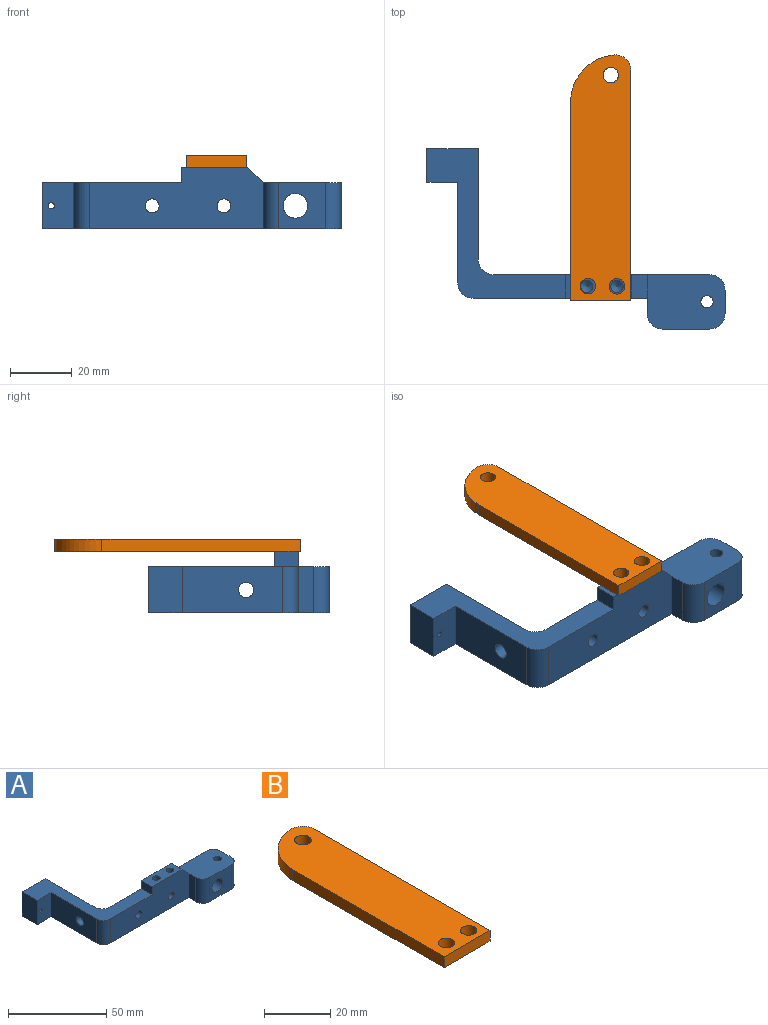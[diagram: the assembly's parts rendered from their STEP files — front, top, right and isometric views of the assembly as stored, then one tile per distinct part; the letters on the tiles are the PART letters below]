
ASSEMBLY  parts=2 mates=1
PART A: 33 faces, bbox 96.8x58.5x20 mm
  f0: plane 32.68x15mm, normal (-1,0,0), area 470.6mm2, adj f7,f8,f17,f27,f32
  f1: plane 25.29x17.65mm, normal (0,0,1), area 417.6mm2, adj f3,f6,f9,f10,f13,f14,f15,f16
  f2: plane 56.5x20mm, normal (0,-1,0), area 935.7mm2, adj f7,f8,f9,f11,f12,f13,f17,f18
  f3: plane 70.15x20mm, normal (0,1,0), area 1090.3mm2, adj f1,f7,f8,f11,f12,f13,f15,f18
  f4: plane 35.9x15mm, normal (1,0,0), area 518.8mm2, adj f5,f7,f8,f26,f32
  f5: plane 16.64x15mm, normal (0,1,0), area 233.8mm2, adj f4,f7,f8,f28,f30,f31
  f6: plane 15x7.65mm, normal (1,0,0), area 114.7mm2, adj f1,f8,f14,f15
  f7: plane 48.54x44.98mm, normal (0,0,1), area 647.4mm2, adj f0,f2,f3,f4,f5,f11,f17,f26
  f8: plane 96.79x58.54mm, normal (0,0,-1), area 1267.7mm2, adj f0,f2,f3,f4,f5,f6,f9,f10
  f9: plane 15x5mm, normal (-1,0,0), area 75mm2, adj f1,f2,f8,f16
  f10: plane 15.29x15mm, normal (0,-1,0), area 179.1mm2, adj f1,f8,f14,f16,f20
  f11: plane 7.65x5mm, normal (-1,0,0), area 38.2mm2, adj f2,f3,f7,f12
  f12: plane 21.52x7.65mm, normal (0,0,1), area 139.4mm2, adj f2,f3,f11,f13,f23,f25
  f13: plane 7.65x5mm, normal (0.71,0,0.71), area 54.1mm2, adj f1,f2,f3,f12
  f14: cylinder r=5mm len=15mm, axis (0,0,-1), area 117.8mm2, adj f1,f6,f8,f10
  f15: cylinder r=5mm len=15mm, axis (0,0,-1), area 117.8mm2, adj f1,f3,f6,f8
  f16: cylinder r=5mm len=15mm, axis (0,0,1), area 117.8mm2, adj f1,f8,f9,f10
  f17: cylinder r=5mm len=15mm, axis (0,0,-1), area 117.8mm2, adj f0,f2,f7,f8
  f18: cylinder r=2.25mm len=7.65mm, axis (0,1,0), area 108.1mm2, adj f2,f3
  f19: cylinder r=2.25mm len=7.65mm, axis (0,1,0), area 108.1mm2, adj f2,f3
  f20: cylinder r=4mm len=17.65mm, axis (0,1,0), area 443.5mm2, adj f3,f10
  f21: cylinder r=2mm len=15mm, axis (0,0,1), area 188.5mm2, adj f1,f8
  f22: cone r=0mm half-angle=59deg, axis (0,0,1), area 14.7mm2, adj f23
  f23: cylinder r=2mm len=10mm, axis (0,0,1), area 125.7mm2, adj f12,f22
  f24: cone r=0mm half-angle=59deg, axis (0,0,1), area 14.7mm2, adj f25
  f25: cylinder r=2mm len=10mm, axis (0,0,1), area 125.7mm2, adj f12,f24
  f26: cylinder r=5mm len=15mm, axis (0,0,-1), area 117.8mm2, adj f3,f4,f7,f8
  f27: plane 15x10mm, normal (0,-1,0), area 146.9mm2, adj f0,f7,f8,f28,f31
  f28: plane 15x10.86mm, normal (-1,0,0), area 162.9mm2, adj f5,f7,f8,f27
  f29: cone r=0mm half-angle=59deg, axis (0,1,0), area 14.7mm2, adj f30
  f30: cylinder r=2mm len=8mm, axis (0,1,0), area 100.5mm2, adj f5,f29
  f31: cylinder r=1mm len=10.86mm, axis (0,1,0), area 68.2mm2, adj f5,f27
  f32: cylinder r=2.5mm len=6.64mm, axis (-1,0,0), area 104.2mm2, adj f0,f4
PART B: 10 faces, bbox 19.6x79.7x4 mm
  f0: plane 64.38x4mm, normal (-1,0,0), area 257.5mm2, adj f2,f3,f4,f7
  f1: plane 74.65x4mm, normal (1,0,0), area 298.6mm2, adj f2,f3,f5,f7
  f2: plane 79.65x19.55mm, normal (0,0,1), area 1443.3mm2, adj f0,f1,f4,f5,f6,f7,f8,f9
  f3: plane 79.65x19.55mm, normal (0,0,-1), area 1443.3mm2, adj f0,f1,f4,f5,f6,f7,f8,f9
  f4: cylinder r=15.29mm len=15.25mm, axis (0,0,1), area 91.7mm2, adj f0,f2,f3,f5
  f5: cylinder r=5mm len=5.36mm, axis (0,0,1), area 32.9mm2, adj f1,f2,f3,f4
  f6: cylinder r=2.5mm len=5mm, axis (0,0,1), area 62.8mm2, adj f2,f3
  f7: plane 19.55x4mm, normal (0,-1,0), area 78.2mm2, adj f0,f1,f2,f3
  f8: cylinder r=2.5mm len=5mm, axis (0,0,1), area 62.8mm2, adj f2,f3
  f9: cylinder r=2.5mm len=5mm, axis (0,0,1), area 62.8mm2, adj f2,f3
PLACE A at identity
PLACE B t=(54.7,83.41,20)mm
MATE fastened B.f9 <-> A.f24  axis (0,0,-1) through (9.82,-3.82,20)mm
